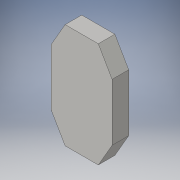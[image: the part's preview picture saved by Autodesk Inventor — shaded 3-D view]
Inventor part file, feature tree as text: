
AUTODESK INVENTOR PART (.ipt)
format: ipt  version: 2016 (Build 200138000, 138)  size: 97,280 bytes
history: native  units: in
note: dims shown in document units (in); Inventor stores cm internally (conversion verified against a paired STEP export)
features: sketch x2, extrude x1
ambient origin geometry x8: Origin, YZ Plane, XZ Plane, XY Plane, X Axis, Y Axis, Z Axis, Center Point
bodies: Solid1 (feature_tree)
feature tree (3):
  sketch  "Sketch1"  dims[d3=6.0in d4=6.0in]
  extrude  "Extrusion1"  Depth=6.0in
  sketch  "Sketch2"  dims[d8=6.0in d9=0.0in d10=20.6795in d11=20.6795in d15=12.0in d16=8.6603in]
